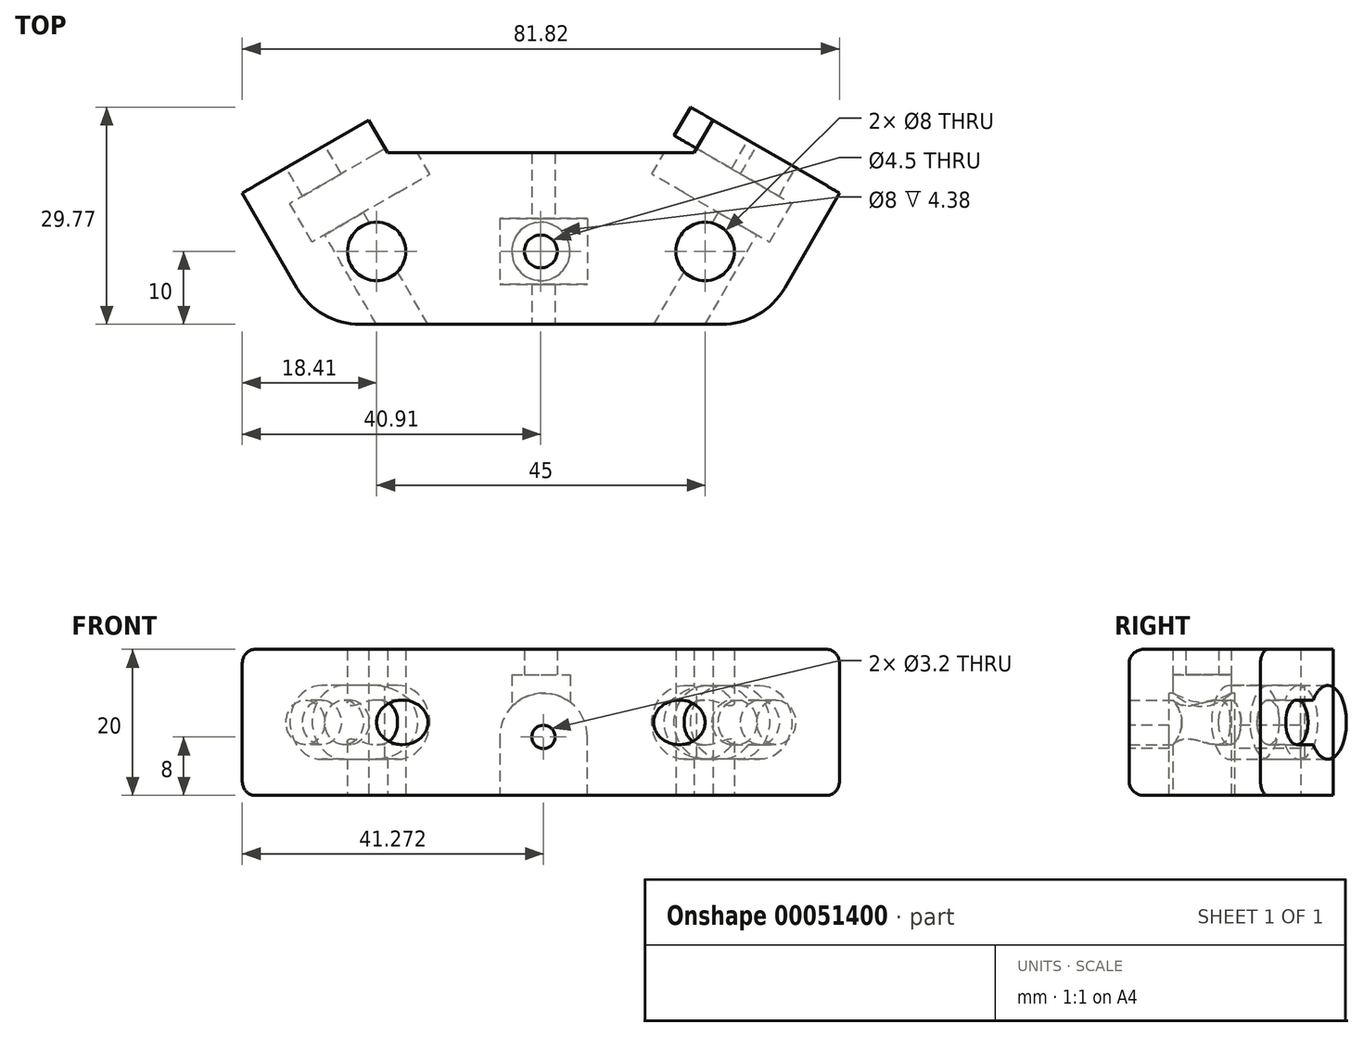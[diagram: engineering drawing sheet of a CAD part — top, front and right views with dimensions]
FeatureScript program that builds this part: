
annotation { "Feature Type Name" : "Feature", "Feature Type Description" : "" }
export const myFeature = defineFeature(function(context is Context, id is Id, definition is map)
    precondition{}
    {
        {
            var Q0;
            Q0=qCreatedBy(makeId("Top.planeOp"),FACE);
            var sketch = newSketch(context, id + "F0", { "sketchPlane" : qUnion([Q0])});
            skLineSegment(sketch, "E0", {"start": v(-22.5, 0) * mm, "end": v(22.5, 0) * mm, "construction": true});
            skCircle(sketch, "E1", {"center": v(22.5, 0) * mm, "radius": 4 * mm});
            skCircle(sketch, "E2", {"center": v(-22.5, 0) * mm, "radius": 4 * mm});
            skLineSegment(sketch, "E3", {"start": v(0, 0) * mm, "end": v(0, 13.5) * mm, "construction": true});
            skLineSegment(sketch, "E4", {"start": v(-21, 13.5) * mm, "end": v(21, 13.5) * mm});
            skLineSegment(sketch, "E5", {"start": v(23.6, 18) * mm, "end": v(40.91, 8) * mm});
            skLineSegment(sketch, "E6", {"start": v(40.91, 8) * mm, "end": v(33.41, -5) * mm});
            skLineSegment(sketch, "E7", {"start": v(24.75, -10) * mm, "end": v(-24.75, -10) * mm});
            skLineSegment(sketch, "E8", {"start": v(0, -10) * mm, "end": v(0, 0) * mm, "construction": true});
            skLineSegment(sketch, "E9", {"start": v(23.6, 18) * mm, "end": v(21, 13.5) * mm});
            skLineSegment(sketch, "E10", {"start": v(22.5, 0) * mm, "end": v(30.56, 13.97) * mm, "construction": true});
            skArc(sketch, "E11", {"start": v(33.41, -5) * mm, "mid": v(29.75, -8.66) * mm, "end": v(24.75, -10) * mm});
            skArc(sketch, "E12.MirrorCS", {"start": v(-33.41, -5) * mm, "mid": v(-29.75, -8.66) * mm, "end": v(-24.75, -10) * mm});
            skLineSegment(sketch, "E13.MirrorCS", {"start": v(-40.91, 8) * mm, "end": v(-33.41, -5) * mm});
            skLineSegment(sketch, "E14.MirrorCS", {"start": v(-23.6, 18) * mm, "end": v(-21, 13.5) * mm});
            skLineSegment(sketch, "E15.MirrorCS", {"start": v(-23.6, 18) * mm, "end": v(-40.91, 8) * mm});
            skSolve(sketch);
        }
        {
            var Q0;
            Q0=qSketchRegion(id+"F0",true);
            extrude(context, id + "F1", {"entities" : qUnion([Q0]), "endBound" : BoundingType.SYMMETRIC, "depth" : 20 * mm});
        }
        {
            var Q0;
            Q0=makeQuery(id+"F1.opExtrude","SWEPT_FACE",FACE,{"disambiguationData":[OSD([sQuery(id+"F0.wireOp",EDGE,"E5")])]});
            var sketch = newSketch(context, id + "F2", { "sketchPlane" : qUnion([Q0])});
            skLineSegment(sketch, "E16", {"start": v(-21.44, 10) * mm, "end": v(-21.44, -10) * mm, "construction": true});
            skPoint(sketch, "E17", {"position": v(-21.44, 0) * mm});
            skSolve(sketch);
        }
        {
            var Q0;
            Q0=makeQuery(id+"F1.opExtrude","SWEPT_FACE",FACE,{"disambiguationData":[OSD([sQuery(id+"F0.wireOp",EDGE,"E15.MirrorCS")])]});
            var sketch = newSketch(context, id + "F3", { "sketchPlane" : qUnion([Q0])});
            skLineSegment(sketch, "E18", {"start": v(21.44, 10) * mm, "end": v(21.44, -10) * mm, "construction": true});
            skPoint(sketch, "E19", {"position": v(21.44, 0) * mm});
            skSolve(sketch);
        }
        {
            var Q0;
            Q0=sQuery(id+"F2.wireOp",VERTEX,"E17");
            var Q1;
            Q1=sQuery(id+"F3.wireOp",VERTEX,"E19");
            var Q2;
            Q2=makeQuery(id+"F1.opExtrude","SWEPT_BODY",BODY,{"disambiguationData":[OSD([sQuery(id+"F0.wireOp",EDGE,"E1"),sQuery(id+"F0.wireOp",EDGE,"E2"),sQuery(id+"F0.wireOp",EDGE,"E4"),sQuery(id+"F0.wireOp",EDGE,"E5"),sQuery(id+"F0.wireOp",EDGE,"E6"),sQuery(id+"F0.wireOp",EDGE,"E7"),sQuery(id+"F0.wireOp",EDGE,"E9"),sQuery(id+"F0.wireOp",EDGE,"E11"),sQuery(id+"F0.wireOp",EDGE,"E12.MirrorCS"),sQuery(id+"F0.wireOp",EDGE,"E13.MirrorCS"),sQuery(id+"F0.wireOp",EDGE,"E14.MirrorCS"),sQuery(id+"F0.wireOp",EDGE,"E15.MirrorCS")])]});
            hole(context, id + "F4", {"style" : HoleStyle.SIMPLE, "holeDiameter" : 6.1 * mm, "endStyle" : HoleEndStyle.THROUGH, "locations" : qUnion([Q0, Q1]), "scope" : qUnion([Q2])});
        }
        {
            var Q0;
            Q0=makeQuery(id+"F1.opExtrude","CAP_FACE",FACE,{"disambiguationData":[OSD([sQuery(id+"F0.wireOp",EDGE,"E1"),sQuery(id+"F0.wireOp",EDGE,"E2"),sQuery(id+"F0.wireOp",EDGE,"E4"),sQuery(id+"F0.wireOp",EDGE,"E5"),sQuery(id+"F0.wireOp",EDGE,"E6"),sQuery(id+"F0.wireOp",EDGE,"E7"),sQuery(id+"F0.wireOp",EDGE,"E9"),sQuery(id+"F0.wireOp",EDGE,"E11"),sQuery(id+"F0.wireOp",EDGE,"E12.MirrorCS"),sQuery(id+"F0.wireOp",EDGE,"E13.MirrorCS"),sQuery(id+"F0.wireOp",EDGE,"E14.MirrorCS"),sQuery(id+"F0.wireOp",EDGE,"E15.MirrorCS")])],"isStart":true});
            var sketch = newSketch(context, id + "F5", { "sketchPlane" : qUnion([Q0])});
            skLineSegment(sketch, "E20", {"start": v(0, 10) * mm, "end": v(0, 0) * mm, "construction": true});
            skPoint(sketch, "E20.endSnap0", {"position": v(0, 10) * mm});
            skSolve(sketch);
        }
        {
            var Q0;
            Q0=sQuery(id+"F5.wireOp",VERTEX,"E20.end");
            var Q1;
            Q1=makeQuery(id+"F1.opExtrude","SWEPT_BODY",BODY,{"disambiguationData":[OSD([sQuery(id+"F0.wireOp",EDGE,"E1"),sQuery(id+"F0.wireOp",EDGE,"E2"),sQuery(id+"F0.wireOp",EDGE,"E4"),sQuery(id+"F0.wireOp",EDGE,"E5"),sQuery(id+"F0.wireOp",EDGE,"E6"),sQuery(id+"F0.wireOp",EDGE,"E7"),sQuery(id+"F0.wireOp",EDGE,"E9"),sQuery(id+"F0.wireOp",EDGE,"E11"),sQuery(id+"F0.wireOp",EDGE,"E12.MirrorCS"),sQuery(id+"F0.wireOp",EDGE,"E13.MirrorCS"),sQuery(id+"F0.wireOp",EDGE,"E14.MirrorCS"),sQuery(id+"F0.wireOp",EDGE,"E15.MirrorCS")])]});
            hole(context, id + "F6", {"style" : HoleStyle.SIMPLE, "holeDiameter" : 4.5 * mm, "endStyle" : HoleEndStyle.THROUGH, "locations" : qUnion([Q0]), "scope" : qUnion([Q1])});
        }
        {
            var Q0;
            Q0=makeQuery(id+"F1.opExtrude","SWEPT_FACE",FACE,{"disambiguationData":[OSD([sQuery(id+"F0.wireOp",EDGE,"E5")])]});
            cPlane(context, id + "F7", {"entities" : qUnion([Q0]), "cplaneType" : CPlaneType.OFFSET, "offset" : 4.5 * mm, "oppositeDirection" : true, "width" : 150 * mm, "height" : 150 * mm});
        }
        {
            var Q0;
            Q0=qCreatedBy(id+"F7.planeOp",FACE);
            var sketch = newSketch(context, id + "F8", { "sketchPlane" : qUnion([Q0])});
            skLineSegment(sketch, "E21", {"start": v(-21.44, 0) * mm, "end": v(-12.94, 0) * mm, "construction": true});
            skLineSegment(sketch, "E22", {"start": v(-21.44, 3.05) * mm, "end": v(-17.41, 3.05) * mm, "construction": true});
            skLineSegment(sketch, "E23", {"start": v(-12.94, 5.05) * mm, "end": v(-21.44, 5.05) * mm});
            skLineSegment(sketch, "E24", {"start": v(-21.44, -5.05) * mm, "end": v(-21.44, -5.05) * mm});
            skArc(sketch, "E25", {"start": v(-12.94, 5.05) * mm, "mid": v(-17.99, 0) * mm, "end": v(-12.94, -5.05) * mm, "construction": true});
            skArc(sketch, "E26", {"start": v(-12.94, -5.05) * mm, "mid": v(-7.89, 0) * mm, "end": v(-12.94, 5.05) * mm});
            skLineSegment(sketch, "E27", {"start": v(-21.44, 5.05) * mm, "end": v(-21.44, 5.05) * mm});
            skLineSegment(sketch, "E28", {"start": v(-21.44, -5.05) * mm, "end": v(-12.94, -5.05) * mm});
            skArc(sketch, "E29", {"start": v(-21.44, 5.05) * mm, "mid": v(-26.49, 0) * mm, "end": v(-21.44, -5.05) * mm});
            skArc(sketch, "E30", {"start": v(-21.44, -5.05) * mm, "mid": v(-16.39, 0) * mm, "end": v(-21.44, 5.05) * mm, "construction": true});
            skSolve(sketch);
        }
        {
            var Q0;
            Q0=qSketchRegion(id+"F8",true);
            extrude(context, id + "F9", {"entities" : qUnion([Q0]), "oppositeDirection" : true, "depth" : 6.1 * mm});
        }
        {
            var Q0;
            Q0=makeQuery(id+"F1.opExtrude","SWEPT_FACE",FACE,{"disambiguationData":[OSD([sQuery(id+"F0.wireOp",EDGE,"E5")])]});
            var sketch = newSketch(context, id + "F10", { "sketchPlane" : qUnion([Q0])});
            skArc(sketch, "E31.0", {"start": v(-21.44, 3.05) * mm, "mid": v(-24.49, 0) * mm, "end": v(-21.44, -3.05) * mm});
            skArc(sketch, "E32", {"start": v(-16.96, -3.05) * mm, "mid": v(-7.89, 0) * mm, "end": v(-16.96, 3.05) * mm});
            skPoint(sketch, "E32.centerSnap0", {"position": v(-31.44, 0) * mm});
            skLineSegment(sketch, "E33", {"start": v(-21.44, 3.05) * mm, "end": v(-16.96, 3.05) * mm});
            skLineSegment(sketch, "E34", {"start": v(-21.44, -3.05) * mm, "end": v(-16.96, -3.05) * mm});
            skSolve(sketch);
        }
        {
            var Q0;
            Q0=qSketchRegion(id+"F10",true);
            var Q1;
            Q1=makeQuery(id+"F9.boolean.opBoolean","COPY",FACE,{"derivedFrom":makeQuery(id+"F9.opExtrude","CAP_FACE",FACE,{"disambiguationData":[OSD([sQuery(id+"F8.wireOp",EDGE,"E23"),sQuery(id+"F8.wireOp",EDGE,"E26"),sQuery(id+"F8.wireOp",EDGE,"E28"),sQuery(id+"F8.wireOp",EDGE,"E29")])],"isStart":false})});
            var Q2;
            Q2=makeQuery(id+"F9.opExtrude","SWEPT_BODY",BODY,{"disambiguationData":[OSD([sQuery(id+"F8.wireOp",EDGE,"E23"),sQuery(id+"F8.wireOp",EDGE,"E26"),sQuery(id+"F8.wireOp",EDGE,"E28"),sQuery(id+"F8.wireOp",EDGE,"E29")])]});
            extrude(context, id + "F11", {"entities" : qUnion([Q0]), "endBound" : BoundingType.UP_TO_BODY, "oppositeDirection" : true, "endBoundEntityFace" : qUnion([Q1]), "endBoundEntityBody" : qUnion([Q2]), "depth" : 25 * mm});
        }
        {
            var Q0;
            Q0=makeQuery(id+"F9.opExtrude","SWEPT_BODY",BODY,{"disambiguationData":[OSD([sQuery(id+"F8.wireOp",EDGE,"E23"),sQuery(id+"F8.wireOp",EDGE,"E26"),sQuery(id+"F8.wireOp",EDGE,"E28"),sQuery(id+"F8.wireOp",EDGE,"E29")])]});
            var Q1;
            Q1=makeQuery(id+"FIZzarfgEjNprrR_2.opPattern","COPY",BODY,{"derivedFrom":makeQuery(id+"F9.opExtrude","SWEPT_BODY",BODY,{"disambiguationData":[OSD([sQuery(id+"F8.wireOp",EDGE,"E23"),sQuery(id+"F8.wireOp",EDGE,"E26"),sQuery(id+"F8.wireOp",EDGE,"E28"),sQuery(id+"F8.wireOp",EDGE,"E29")])]}),"instanceName":"1"});
            var Q2;
            Q2=qCreatedBy(makeId("Right.planeOp"),FACE);
            mirror(context, id + "F12", {"entities" : qUnion([Q0, Q1]), "mirrorPlane" : qUnion([Q2])});
        }
        {
            var Q0;
            Q0=makeQuery(id+"F9.opExtrude","SWEPT_BODY",BODY,{"disambiguationData":[OSD([sQuery(id+"F8.wireOp",EDGE,"E23"),sQuery(id+"F8.wireOp",EDGE,"E26"),sQuery(id+"F8.wireOp",EDGE,"E28"),sQuery(id+"F8.wireOp",EDGE,"E29")])]});
            var Q1;
            Q1=makeQuery(id+"F12.opPattern","COPY",BODY,{"derivedFrom":makeQuery(id+"F9.opExtrude","SWEPT_BODY",BODY,{"disambiguationData":[OSD([sQuery(id+"F8.wireOp",EDGE,"E23"),sQuery(id+"F8.wireOp",EDGE,"E26"),sQuery(id+"F8.wireOp",EDGE,"E28"),sQuery(id+"F8.wireOp",EDGE,"E29")])]}),"instanceName":"1"});
            var Q2;
            Q2=makeQuery(id+"F1.opExtrude","SWEPT_BODY",BODY,{"disambiguationData":[OSD([sQuery(id+"F0.wireOp",EDGE,"E1"),sQuery(id+"F0.wireOp",EDGE,"E2"),sQuery(id+"F0.wireOp",EDGE,"E4"),sQuery(id+"F0.wireOp",EDGE,"E5"),sQuery(id+"F0.wireOp",EDGE,"E6"),sQuery(id+"F0.wireOp",EDGE,"E7"),sQuery(id+"F0.wireOp",EDGE,"E9"),sQuery(id+"F0.wireOp",EDGE,"E11"),sQuery(id+"F0.wireOp",EDGE,"E12.MirrorCS"),sQuery(id+"F0.wireOp",EDGE,"E13.MirrorCS"),sQuery(id+"F0.wireOp",EDGE,"E14.MirrorCS"),sQuery(id+"F0.wireOp",EDGE,"E15.MirrorCS")])]});
            booleanBodies(context, id + "F13", {"operationType" : BooleanOperationType.SUBTRACTION, "tools" : qUnion([Q0, Q1]), "targets" : qUnion([Q2])});
        }
        {
            var Q0;
            Q0=makeQuery(id+"F1.opExtrude","CAP_EDGE",EDGE,{"disambiguationData":[OSD([sQuery(id+"F0.wireOp",EDGE,"E13.MirrorCS")])],"isStart":false});
            var Q1;
            Q1=makeQuery(id+"F1.opExtrude","CAP_EDGE",EDGE,{"disambiguationData":[OSD([sQuery(id+"F0.wireOp",EDGE,"E13.MirrorCS")])],"isStart":true});
            fillet(context, id + "F14", {"entities" : qUnion([Q0, Q1]), "radius" : 2 * mm, "tangentPropagation" : true, "allowEdgeOverflow" : false});
        }
        {
            var Q0;
            Q0=qCreatedBy(makeId("Front.planeOp"),FACE);
            var sketch = newSketch(context, id + "F15", { "sketchPlane" : qUnion([Q0])});
            skArc(sketch, "E35", {"start": v(6.36, -2) * mm, "mid": v(0.36, 4) * mm, "end": v(-5.64, -2) * mm});
            skLineSegment(sketch, "E36", {"start": v(-5.64, -2) * mm, "end": v(-5.64, -10) * mm});
            skLineSegment(sketch, "E37", {"start": v(-5.64, -10) * mm, "end": v(6.36, -10) * mm});
            skLineSegment(sketch, "E38", {"start": v(6.36, -10) * mm, "end": v(6.36, -2) * mm});
            skSolve(sketch);
        }
        {
            var Q0;
            Q0 = qSketchRegion(id + "F15", true);
            extrude(context, id + "F16", {"entities" : qUnion([Q0]), "operationType" : NewBodyOperationType.REMOVE, "endBound" : BoundingType.SYMMETRIC, "oppositeDirection" : true, "depth" : 9 * mm});
        }
        {
            var Q0;
            Q0=makeQuery(id+"F1.opExtrude","SWEPT_FACE",FACE,{"disambiguationData":[OSD([sQuery(id+"F0.wireOp",EDGE,"E7")])]});
            var sketch = newSketch(context, id + "F17", { "sketchPlane" : qUnion([Q0])});
            skCircle(sketch, "E39", {"center": v(0.36, -2) * mm, "radius": 1.6 * mm});
            skSolve(sketch);
        }
        {
            var Q0;
            Q0 = qSketchRegion(id + "F17", true);
            extrude(context, id + "F18", {"entities" : qUnion([Q0]), "operationType" : NewBodyOperationType.REMOVE, "endBound" : BoundingType.THROUGH_ALL, "oppositeDirection" : true, "depth" : 25 * mm});
        }
        {
            var Q0;
            Q0=makeQuery(id+"F1.opExtrude","CAP_FACE",FACE,{"disambiguationData":[OSD([sQuery(id+"F0.wireOp",EDGE,"E1"),sQuery(id+"F0.wireOp",EDGE,"E2"),sQuery(id+"F0.wireOp",EDGE,"E4"),sQuery(id+"F0.wireOp",EDGE,"E5"),sQuery(id+"F0.wireOp",EDGE,"E6"),sQuery(id+"F0.wireOp",EDGE,"E7"),sQuery(id+"F0.wireOp",EDGE,"E9"),sQuery(id+"F0.wireOp",EDGE,"E11"),sQuery(id+"F0.wireOp",EDGE,"E12.MirrorCS"),sQuery(id+"F0.wireOp",EDGE,"E13.MirrorCS"),sQuery(id+"F0.wireOp",EDGE,"E14.MirrorCS"),sQuery(id+"F0.wireOp",EDGE,"E15.MirrorCS")])],"isStart":true});
            var sketch = newSketch(context, id + "F19", { "sketchPlane" : qUnion([Q0])});
            skCircle(sketch, "E40", {"center": v(0, 0) * mm, "radius": 4 * mm});
            skSolve(sketch);
        }
        {
            var Q0;
            Q0 = qSketchRegion(id + "F19", true);
            extrude(context, id + "F20", {"entities" : qUnion([Q0]), "operationType" : NewBodyOperationType.REMOVE, "oppositeDirection" : true, "depth" : 16.5 * mm});
        }
    });
